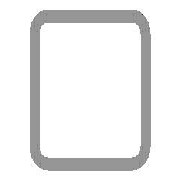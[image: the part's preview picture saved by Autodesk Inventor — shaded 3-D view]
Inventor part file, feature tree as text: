
AUTODESK INVENTOR PART (.ipt)
format: ipt  version: 2016 (Build 200138000, 138)  size: 146,432 bytes
history: native  units: mm (DEFAULTED — no unit token found)
features: other x4, plane x3, sketch x3, split x2
ambient origin geometry x8: Origin, YZ Plane, XZ Plane, XY Plane, X Axis, Y Axis, Z Axis, Center Point
bodies: Solid1 (feature_tree), Body (feature_tree)
feature tree (12):
  parser-record x1  (decoder bookkeeping rows leaked as tree rows — omitted from the tree; the rows remain in map.json)
  other  "Driven Length"
  other  "Start plane"
  other  "End plane"
  plane  "Work Plane4"
  split  "Split1"
  plane  "Work Plane5"
  split  "Split2"
  sketch  "Sketch"  dims[d7=4.0mm d9=25.0mm d11=25.0mm d12=2.0mm d13=0.212132mm d14=309.787868mm d15=12.5mm d16=12.5mm d17=90.0deg d18=309.575736mm]
  sketch  "Sketch3"  dims[d3=309.575736mm]
  plane  "Work Plane3"
  sketch  "Sketch4"  dims[d4=0.0mm]
